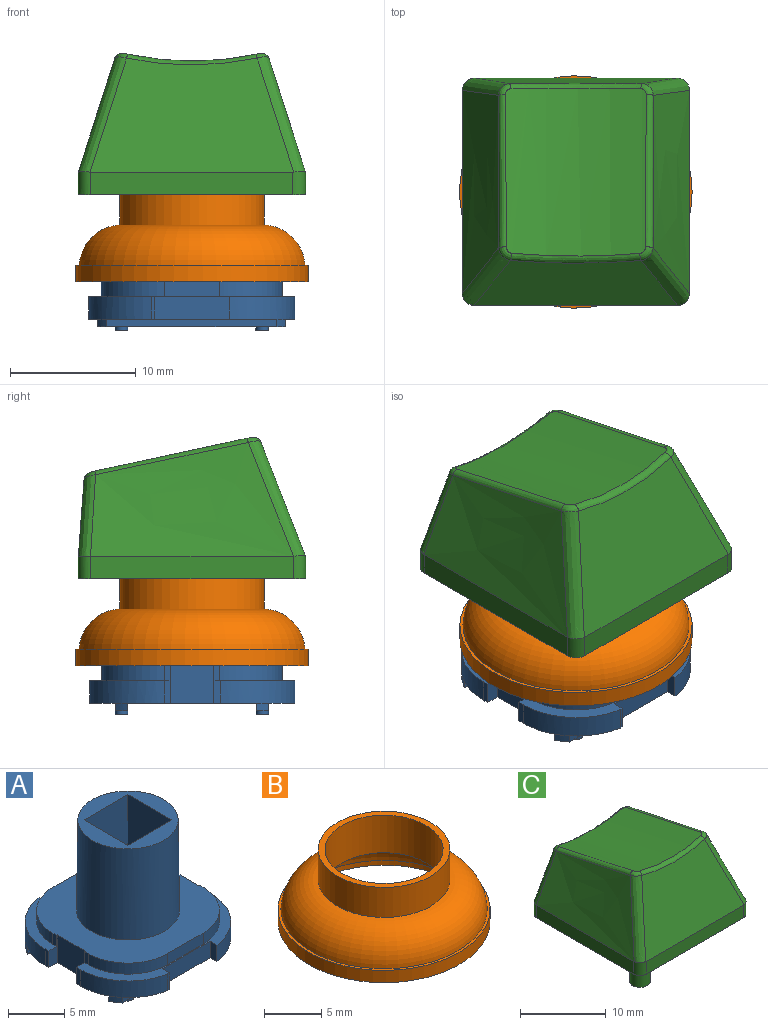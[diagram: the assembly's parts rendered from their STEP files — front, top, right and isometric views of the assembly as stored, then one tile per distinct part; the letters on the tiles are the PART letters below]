
ASSEMBLY  parts=3 mates=2
PART A: 86 faces, bbox 16.4x16.4x13.7 mm
  f0: plane 6x1.8mm, normal (0,1,0), area 10.8mm2, adj f3,f10,f11,f12
  f1: plane 1x1mm, normal (0,0,-1), area 0.8mm2, adj f13
  f2: plane 1x1mm, normal (0,0,-1), area 0.8mm2, adj f14
  f3: plane 1.8x0.85mm, normal (1,0,0), area 1.5mm2, adj f0,f11,f12,f26
  f4: plane 1.2x0.45mm, normal (-1,0,0), area 0.5mm2, adj f5,f11,f27,f28
  f5: revolved ~5x5mm, area 9.4mm2, adj f4,f6,f11,f28
  f6: plane 4.4x1.2mm, normal (0,1,0), area 5.3mm2, adj f5,f7,f11,f28
  f7: revolved ~5x5mm, area 9.4mm2, adj f6,f9,f11,f28
  f8: revolved ~9.8x9.13mm, area 277.6mm2, adj f19,f28
  f9: plane 1.2x0.45mm, normal (1,0,0), area 0.5mm2, adj f7,f11,f28,f29
  f10: plane 1.8x0.85mm, normal (-1,0,0), area 1.5mm2, adj f0,f11,f12,f31
  f11: plane 16.4x6.4mm, normal (0,0,1), area 17.2mm2, adj f0,f3,f4,f5,f6,f7,f9,f10
  f12: plane 13.52x2.05mm, normal (0,0,-1), area 17.2mm2, adj f0,f3,f10,f15,f26,f31
  f13: revolved ~1x1mm, area 0.9mm2, adj f1,f32,f33
  f14: revolved ~1x1mm, area 0.9mm2, adj f2,f33,f34
  f15: plane 13.52x0.6mm, normal (0,1,0), area 8.1mm2, adj f12,f32,f33,f34,f35,f36
  f16: plane 2.8x0.75mm, normal (0,0,-1), area 2.1mm2, adj f40,f41,f42,f43
  f17: plane 2.8x0.75mm, normal (0,0,-1), area 2.1mm2, adj f44,f45,f46,f47
  f18: plane 2.8x0.75mm, normal (0,0,-1), area 2.1mm2, adj f48,f49,f50,f51
  f19: plane 8.9x8.9mm, normal (0,0,1), area 32mm2, adj f8,f43,f47,f51,f52
  f20: plane 2.8x0.75mm, normal (0,0,-1), area 2.1mm2, adj f37,f38,f39,f52
  f21: revolved ~5x5mm, area 9.4mm2, adj f22,f24,f28,f55
  f22: plane 4.4x1.2mm, normal (0,-1,0), area 5.3mm2, adj f21,f23,f28,f55
  f23: revolved ~5x5mm, area 9.4mm2, adj f22,f28,f53,f55
  f24: plane 1.2x0.45mm, normal (1,0,0), area 0.5mm2, adj f21,f28,f55,f57
  f25: plane 1.8x0.45mm, normal (-1,0,0), area 0.8mm2, adj f11,f26,f27,f58
  f26: revolved ~5.95x5.2mm, area 15.5mm2, adj f3,f11,f12,f25,f35,f58
  f27: plane 3x1.1mm, normal (0,-1,0), area 2.1mm2, adj f4,f11,f25,f28,f58,f59,f72
  f28: plane 14.4x14.4mm, normal (0,0,1), area 119.7mm2, adj f4,f5,f6,f7,f8,f9,f21,f22
  f29: plane 3x1.1mm, normal (0,-1,0), area 2.1mm2, adj f9,f11,f28,f30,f60,f61,f72
  f30: plane 1.8x0.45mm, normal (1,0,0), area 0.8mm2, adj f11,f29,f31,f61
  f31: revolved ~5.95x5.2mm, area 15.5mm2, adj f10,f11,f12,f30,f36,f61
  f32: plane 1.86x1mm, normal (0,0,-1), area 1.1mm2, adj f13,f15,f36,f62
  f33: plane 11.2x1mm, normal (0,0,-1), area 10.4mm2, adj f13,f14,f15,f62
  f34: plane 1.85x1mm, normal (0,0,-1), area 1.1mm2, adj f14,f15,f35,f62
  f35: revolved ~1x0.69mm, area 0.7mm2, adj f15,f26,f34,f62
  f36: revolved ~1x0.69mm, area 0.7mm2, adj f15,f31,f32,f62
  f37: plane 5.9x0.75mm, normal (0,1,0), area 4.4mm2, adj f20,f38,f52,f63
  f38: plane 5.9x2.8mm, normal (1,0,0), area 16.5mm2, adj f20,f37,f39,f63
  f39: plane 5.9x0.75mm, normal (0,-1,0), area 4.4mm2, adj f20,f38,f52,f63
  f40: plane 5.9x0.75mm, normal (1,0,0), area 4.4mm2, adj f16,f41,f43,f63
  f41: plane 5.9x2.8mm, normal (0,-1,0), area 16.5mm2, adj f16,f40,f42,f63
  f42: plane 5.9x0.75mm, normal (-1,0,0), area 4.4mm2, adj f16,f41,f43,f63
  f43: plane 12.8x5.5mm, normal (0,-1,0), area 53.9mm2, adj f16,f19,f40,f42,f47,f52,f63
  f44: plane 5.9x0.75mm, normal (0,-1,0), area 4.4mm2, adj f17,f45,f47,f63
  f45: plane 5.9x2.8mm, normal (-1,0,0), area 16.5mm2, adj f17,f44,f46,f63
  f46: plane 5.9x0.75mm, normal (0,1,0), area 4.4mm2, adj f17,f45,f47,f63
  f47: plane 12.8x5.5mm, normal (-1,0,0), area 53.9mm2, adj f17,f19,f43,f44,f46,f51,f63
  f48: plane 5.9x0.75mm, normal (-1,0,0), area 4.4mm2, adj f18,f49,f51,f63
  f49: plane 5.9x2.8mm, normal (0,1,0), area 16.5mm2, adj f18,f48,f50,f63
  f50: plane 5.9x0.75mm, normal (1,0,0), area 4.4mm2, adj f18,f49,f51,f63
  f51: plane 12.8x5.5mm, normal (0,1,0), area 53.9mm2, adj f18,f19,f47,f48,f50,f52,f63
  f52: plane 12.8x5.5mm, normal (1,0,0), area 53.9mm2, adj f19,f20,f37,f39,f43,f51,f63
  f53: plane 1.2x0.45mm, normal (-1,0,0), area 0.5mm2, adj f23,f28,f55,f64
  f54: plane 1.8x0.2mm, normal (0,-1,0), area 0.4mm2, adj f55,f66,f70,f77
  f55: plane 16.4x6.45mm, normal (0,0,1), area 17.6mm2, adj f21,f22,f23,f24,f53,f54,f56,f57
  f56: plane 1.8x0.45mm, normal (1,0,0), area 0.8mm2, adj f55,f57,f69,f71
  f57: plane 3x1.1mm, normal (0,1,0), area 2.1mm2, adj f24,f28,f55,f56,f60,f71,f72
  f58: plane 3.35x1.93mm, normal (0,0,-1), area 3.5mm2, adj f25,f26,f27,f62,f72
  f59: plane 3.5x3mm, normal (-1,0,0), area 10.5mm2, adj f27,f28,f64,f72
  f60: plane 3.5x3mm, normal (1,0,0), area 10.5mm2, adj f28,f29,f57,f72
  f61: plane 3.35x1.93mm, normal (0,0,-1), area 3.5mm2, adj f29,f30,f31,f62,f72
  f62: plane 14.91x0.6mm, normal (0,-1,0), area 8.9mm2, adj f32,f33,f34,f35,f36,f58,f61,f72
  f63: plane 9.2x9.2mm, normal (0,0,-1), area 27.8mm2, adj f37,f38,f39,f40,f41,f42,f43,f44
  f64: plane 3x1.1mm, normal (0,1,0), area 2.1mm2, adj f28,f53,f55,f59,f65,f72,f73
  f65: plane 1.8x0.53mm, normal (-1,0,0), area 1mm2, adj f55,f64,f70,f73
  f66: plane 1.8x0.9mm, normal (1,0,0), area 1.6mm2, adj f54,f55,f67,f77
  f67: plane 6x1.8mm, normal (0,-1,0), area 10.8mm2, adj f55,f66,f68,f77
  f68: plane 1.8x0.85mm, normal (-1,0,0), area 1.5mm2, adj f55,f67,f69,f77
  f69: revolved ~5.95x5.2mm, area 15.5mm2, adj f55,f56,f68,f71,f75,f77
  f70: revolved ~5.92x5mm, area 15.2mm2, adj f54,f55,f65,f73,f77,f78
  f71: plane 3.35x1.93mm, normal (0,0,-1), area 3.5mm2, adj f56,f57,f69,f72,f79
  f72: plane 14.4x10.2mm, normal (0,0,-1), area 76.3mm2, adj f27,f29,f57,f58,f59,f60,f61,f62
  f73: plane 3.35x1.93mm, normal (0,0,-1), area 3.6mm2, adj f64,f65,f70,f72,f79
  f74: plane 1x1mm, normal (0,0,-1), area 0.8mm2, adj f80
  f75: revolved ~1x0.69mm, area 0.7mm2, adj f69,f76,f79,f81
  f76: plane 1.86x1mm, normal (0,0,-1), area 1.1mm2, adj f75,f79,f80,f81
  f77: plane 13.59x2.1mm, normal (0,0,-1), area 17.5mm2, adj f54,f66,f67,f68,f69,f70,f81
  f78: revolved ~1x0.67mm, area 0.7mm2, adj f70,f79,f81,f82
  f79: plane 14.95x0.6mm, normal (0,1,0), area 9mm2, adj f71,f72,f73,f75,f76,f78,f82,f83
  f80: revolved ~1x1mm, area 0.9mm2, adj f74,f76,f83
  f81: plane 13.59x0.6mm, normal (0,-1,0), area 8.2mm2, adj f75,f76,f77,f78,f82,f83
  f82: plane 1.9x1mm, normal (0,0,-1), area 1.2mm2, adj f78,f79,f81,f84
  f83: plane 11.2x1mm, normal (0,0,-1), area 10.4mm2, adj f79,f80,f81,f84
  f84: revolved ~1x1mm, area 0.9mm2, adj f82,f83,f85
  f85: plane 1x1mm, normal (0,0,-1), area 0.8mm2, adj f84
PART B: 9 faces, bbox 19.5x19.5x7.7 mm
  f0: cylinder r=9.25mm len=18.5mm, axis (0,0,1), area 76.2mm2, adj f1,f8
  f1: plane 18.5x18.5mm, normal (0,0,-1), area 41.8mm2, adj f0,f2
  f2: cylinder r=8.5mm len=17mm, axis (0,0,1), area 27.5mm2, adj f1,f3
  f3: torus R=5.16mm, axis (0,0,1), area 232.3mm2, adj f2,f4
  f4: cylinder r=5.15mm len=10.3mm, axis (0,0,1), area 129.4mm2, adj f3,f5
  f5: plane 11.5x11.5mm, normal (0,0,1), area 20.5mm2, adj f4,f6
  f6: cylinder r=5.75mm len=11.5mm, axis (0,0,1), area 115.6mm2, adj f5,f7
  f7: torus R=5.6mm, axis (0,0,1), area 243.6mm2, adj f6,f8
  f8: plane 18.5x18.5mm, normal (0,0,1), area 14.3mm2, adj f0,f7
PART C: 42 faces, bbox 21.1x23x23.7 mm
  f0: plane 18.1x18.1mm, normal (0,0,-1), area 67.5mm2, adj f1,f2,f3,f4,f10,f12,f14,f16
  f1: plane 16.1x1.8mm, normal (1,0,0), area 29mm2, adj f0,f8,f10,f16
  f2: plane 16.11x1.81mm, normal (0,1,0), area 29mm2, adj f0,f5,f14,f15,f16,f17
  f3: plane 16.1x1.8mm, normal (-1,0,0), area 29mm2, adj f0,f6,f12,f14
  f4: plane 16.1x1.8mm, normal (0,-1,0), area 29mm2, adj f0,f7,f10,f12
  f5: plane 15.98x6.12mm, normal (0,1,0.07), area 77mm2, adj f2,f15,f17,f20
  f6: bspline ~18.1x9.7mm, area 119.5mm2, adj f3,f12,f13,f14,f15,f19
  f7: plane 16.23x9.1mm, normal (0,-0.93,0.36), area 126mm2, adj f4,f10,f11,f12,f13,f23
  f8: bspline ~18.1x9.7mm, area 119.6mm2, adj f1,f10,f11,f16,f17,f24
  f9: cylinder r=22.9mm len=13.26mm, axis (0,0.98,-0.21), area 150.5mm2, adj f18,f19,f20,f21,f22,f23,f24,f25
  f10: cylinder r=1mm len=1.86mm, axis (0,0,-1), area 2.9mm2, adj f0,f1,f4,f7,f8,f11
  f11: bspline ~11.76x5.48mm, area 15.2mm2, adj f7,f8,f10,f25
  f12: cylinder r=1mm len=1.86mm, axis (0,0,1), area 2.9mm2, adj f0,f3,f4,f6,f7,f13
  f13: bspline ~11.82x5.5mm, area 15.2mm2, adj f6,f7,f12,f21
  f14: cylinder r=1mm len=1.81mm, axis (0,0,-1), area 2.8mm2, adj f0,f2,f3,f6,f15
  f15: bspline ~8.75x4.63mm, area 10.5mm2, adj f2,f5,f6,f14,f18
  f16: cylinder r=1mm len=1.81mm, axis (0,0,1), area 2.8mm2, adj f0,f1,f2,f8,f17
  f17: bspline ~8.72x4.61mm, area 10.5mm2, adj f2,f5,f8,f16,f22
  f18: bspline ~1.16x1.04mm, area 0.7mm2, adj f9,f15,f19,f20
  f19: bspline ~19.37x4.53mm, area 9.1mm2, adj f6,f9,f18,f21
  f20: bspline ~10.57x1.07mm, area 6.8mm2, adj f5,f9,f18,f22
  f21: bspline ~1.24x1.16mm, area 0.9mm2, adj f9,f13,f19,f23
  f22: bspline ~1.18x0.98mm, area 0.7mm2, adj f9,f17,f20,f24
  f23: bspline ~10.39x0.86mm, area 7.3mm2, adj f7,f9,f21,f25
  f24: bspline ~19.36x4.52mm, area 9.1mm2, adj f8,f9,f22,f25
  f25: bspline ~1.33x1.09mm, area 0.9mm2, adj f9,f11,f23,f24
  f26: plane 16.13x1.68mm, normal (-1,0,0), area 26.1mm2, adj f0,f27,f29,f32,f33
  f27: plane 16.1x1.76mm, normal (0,-1,0), area 28.4mm2, adj f0,f26,f28,f30,f31,f33
  f28: plane 16.13x1.68mm, normal (1,0,0), area 26.1mm2, adj f0,f27,f29,f31,f32
  f29: plane 16.1x1.61mm, normal (0,1,0), area 25.9mm2, adj f0,f26,f28,f32
  f30: plane 16.32x6.11mm, normal (0,-1,-0.07), area 72.4mm2, adj f27,f31,f33,f34
  f31: offset ~20.1x11.7mm, area 111mm2, adj f27,f28,f30,f32,f34
  f32: plane 16.29x8.73mm, normal (0,0.93,-0.36), area 118.5mm2, adj f26,f28,f29,f31,f33,f34
  f33: offset ~20.1x11.7mm, area 111mm2, adj f26,f27,f30,f32,f34
  f34: cylinder r=23.9mm len=12.45mm, axis (0,0.98,-0.21), area 108mm2, adj f30,f31,f32,f33,f36,f37,f38,f39
  f35: plane 5.3x5.3mm, normal (0,0,-1), area 23.6mm2, adj f36,f37,f38,f39,f40
  f36: plane 14.26x5.36mm, normal (0,1,0), area 74.7mm2, adj f34,f35,f37,f38
  f37: plane 15.34x5.3mm, normal (1,0,0), area 78.3mm2, adj f34,f35,f36,f39
  f38: plane 15.34x5.3mm, normal (-1,0,0), area 78.3mm2, adj f34,f35,f36,f39
  f39: plane 15.41x5.36mm, normal (0,-1,0), area 80.8mm2, adj f34,f35,f37,f38
  f40: cylinder r=1.2mm len=3.5mm, axis (0,0,1), area 26.4mm2, adj f35,f41
  f41: plane 2.4x2.4mm, normal (0,0,-1), area 4.5mm2, adj f40
PLACE A at identity fixed
PLACE B t=(0,0,3)mm
PLACE C t=(0,0,9.9)mm
MATE fastened A.f19 <-> C.f40  axis (0,0,1) through (0,0,12.8)mm
MATE fastened A.f28 <-> B.f0  axis (0,0,1) through (0,0,3)mm
